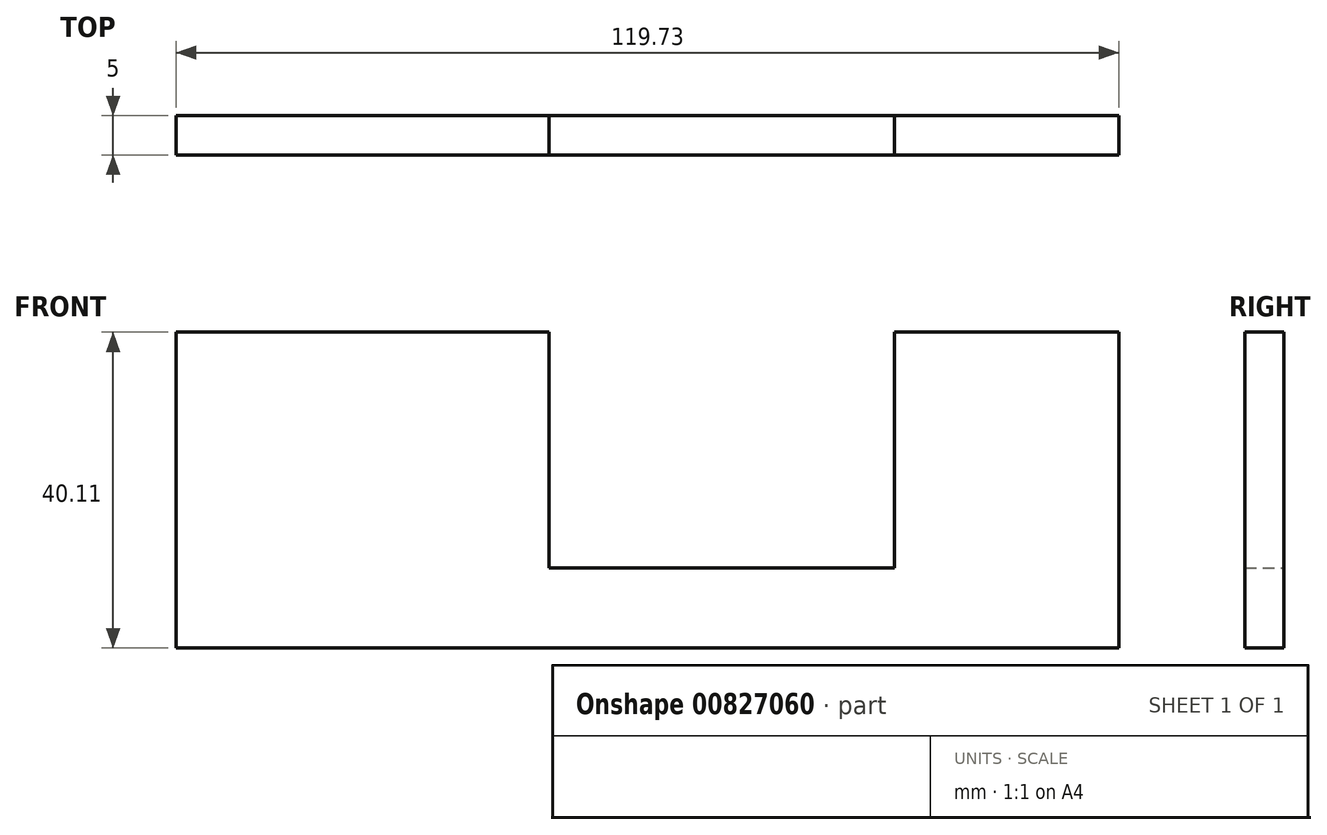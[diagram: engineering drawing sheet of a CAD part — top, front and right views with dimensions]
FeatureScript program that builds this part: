
annotation { "Feature Type Name" : "Feature", "Feature Type Description" : "" }
export const myFeature = defineFeature(function(context is Context, id is Id, definition is map)
    precondition{}
    {
        {
            var Q0;
            Q0=qCreatedBy(makeId("Front.planeOp"),FACE);
            var sketch = newSketch(context, id + "F0", { "sketchPlane" : qUnion([Q0])});
            skLineSegment(sketch, "E0.top", {"start": v(-51.58, -10.03) * mm, "end": v(-7.7, -10.03) * mm});
            skLineSegment(sketch, "E0.left", {"start": v(-51.58, 19.9) * mm, "end": v(-51.58, -10.03) * mm});
            skLineSegment(sketch, "E0.right", {"start": v(-7.7, 19.9) * mm, "end": v(-7.7, -10.03) * mm});
            skLineSegment(sketch, "E1.bottom", {"start": v(-98.95, -20.2) * mm, "end": v(20.78, -20.2) * mm});
            skLineSegment(sketch, "E1.top", {"start": v(-98.95, 19.9) * mm, "end": v(-51.58, 19.9) * mm});
            skLineSegment(sketch, "E1.left", {"start": v(-98.95, -20.2) * mm, "end": v(-98.95, 19.9) * mm});
            skLineSegment(sketch, "E1.right", {"start": v(20.78, -20.2) * mm, "end": v(20.78, 19.9) * mm});
            skLineSegment(sketch, "E2.trimOffspring", {"start": v(-7.7, 19.9) * mm, "end": v(20.78, 19.9) * mm});
            skSolve(sketch);
        }
        {
            var Q0;
            Q0=makeQuery(id+"F0.imprint","IMPRINT",FACE,{"disambiguationData":[TD([[makeQuery(id+"F0.imprint","IMPRINT",EDGE,{"derivedFrom":sQuery(id+"F0.wireOp",EDGE,"E0.top")}),-1.0]])]});
            extrude(context, id + "F1", {"entities" : qUnion([Q0]), "depth" : 5 * mm, "offsetDistance" : 25 * mm});
        }
    });
